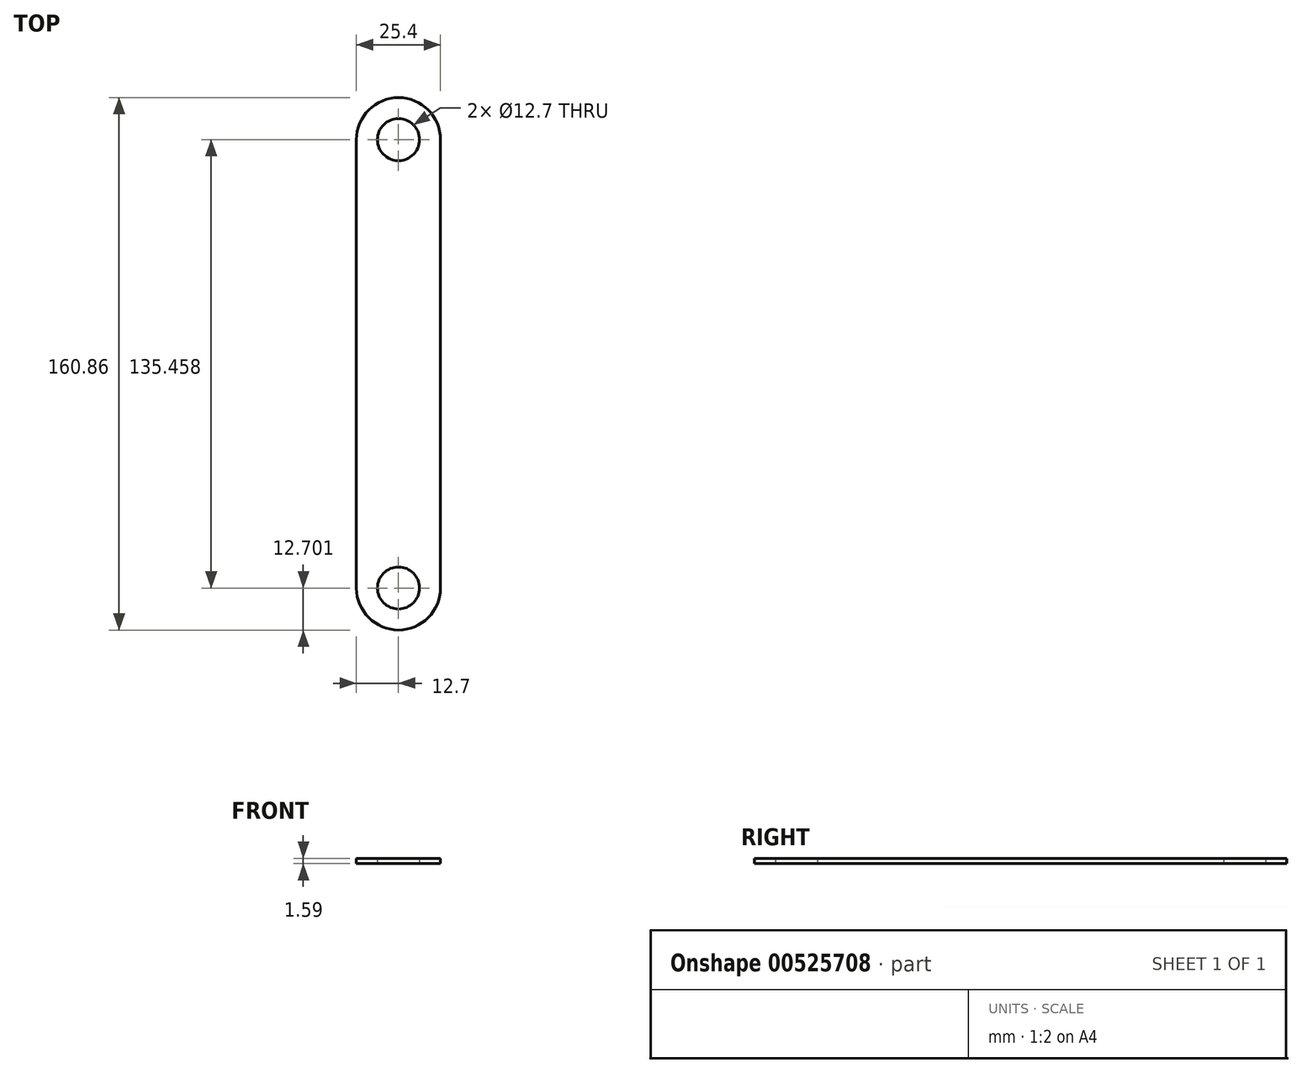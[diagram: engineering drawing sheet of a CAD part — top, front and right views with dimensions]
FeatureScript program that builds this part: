
annotation { "Feature Type Name" : "Feature", "Feature Type Description" : "" }
export const myFeature = defineFeature(function(context is Context, id is Id, definition is map)
    precondition{}
    {
        {
            var Q0;
            Q0=qCreatedBy(makeId("Top.planeOp"),FACE);
            var sketch = newSketch(context, id + "F0", { "sketchPlane" : qUnion([Q0])});
            skLineSegment(sketch, "E0.bottom", {"start": v(-12.7, 67.73) * mm, "end": v(12.7, 67.73) * mm});
            skLineSegment(sketch, "E0.top", {"start": v(-12.7, -67.73) * mm, "end": v(12.7, -67.73) * mm});
            skLineSegment(sketch, "E0.left", {"start": v(-12.7, 67.73) * mm, "end": v(-12.7, -67.73) * mm});
            skLineSegment(sketch, "E0.right", {"start": v(12.7, 67.73) * mm, "end": v(12.7, -67.73) * mm});
            skPoint(sketch, "E0.middle", {"position": v(0, 0) * mm});
            skArc(sketch, "E1", {"start": v(12.7, 67.73) * mm, "mid": v(0, 80.43) * mm, "end": v(-12.7, 67.73) * mm});
            skArc(sketch, "E2", {"start": v(-12.7, -67.73) * mm, "mid": v(0, -80.43) * mm, "end": v(12.7, -67.73) * mm});
            skLineSegment(sketch, "E3", {"start": v(0, 80.43) * mm, "end": v(0, -80.43) * mm});
            skCircle(sketch, "E4", {"center": v(0, 67.73) * mm, "radius": 6.35 * mm});
            skCircle(sketch, "E5", {"center": v(0, -67.73) * mm, "radius": 6.35 * mm});
            skLineSegment(sketch, "E6", {"start": v(0, 74.08) * mm, "end": v(0, -74.08) * mm});
            skSolve(sketch);
        }
        {
            var Q0;
            Q0 = qSketchRegion(id + "F0", true);
            extrude(context, id + "F1", {"entities" : qUnion([Q0]), "depth" : 1.59 * mm, "offsetDistance" : 25.4 * mm});
        }
    });
